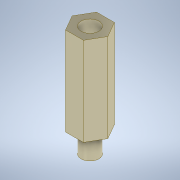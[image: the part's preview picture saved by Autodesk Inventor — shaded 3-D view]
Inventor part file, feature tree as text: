
AUTODESK INVENTOR PART (.ipt)
format: ipt  version: 2021 (Build 250183000, 183)  size: 110,080 bytes
history: native  units: mm
features: extrude x3, sketch x3
ambient origin geometry x8: Origin, YZ Plane, XZ Plane, XY Plane, X Axis, Y Axis, Z Axis, Center Point
bodies: Solid1 (feature_tree)
feature tree (6):
  extrude  "Extrusion1"  Depth=20.0mm TaperAngle=0.0deg
  extrude  "Extrusion2"  Depth=5.0mm TaperAngle=0.0deg
  extrude  "Extrusion3"  Depth=5.0mm TaperAngle=0.0deg
  sketch  "Sketch1"  dims[d0=7.0mm d1=20.0mm d2=0.0mm]
  sketch  "Sketch2"  dims[d3=4.0mm d4=5.0mm d5=0.0mm]
  sketch  "Sketch3"  dims[d6=4.0mm d7=5.0mm d8=0.0mm]
